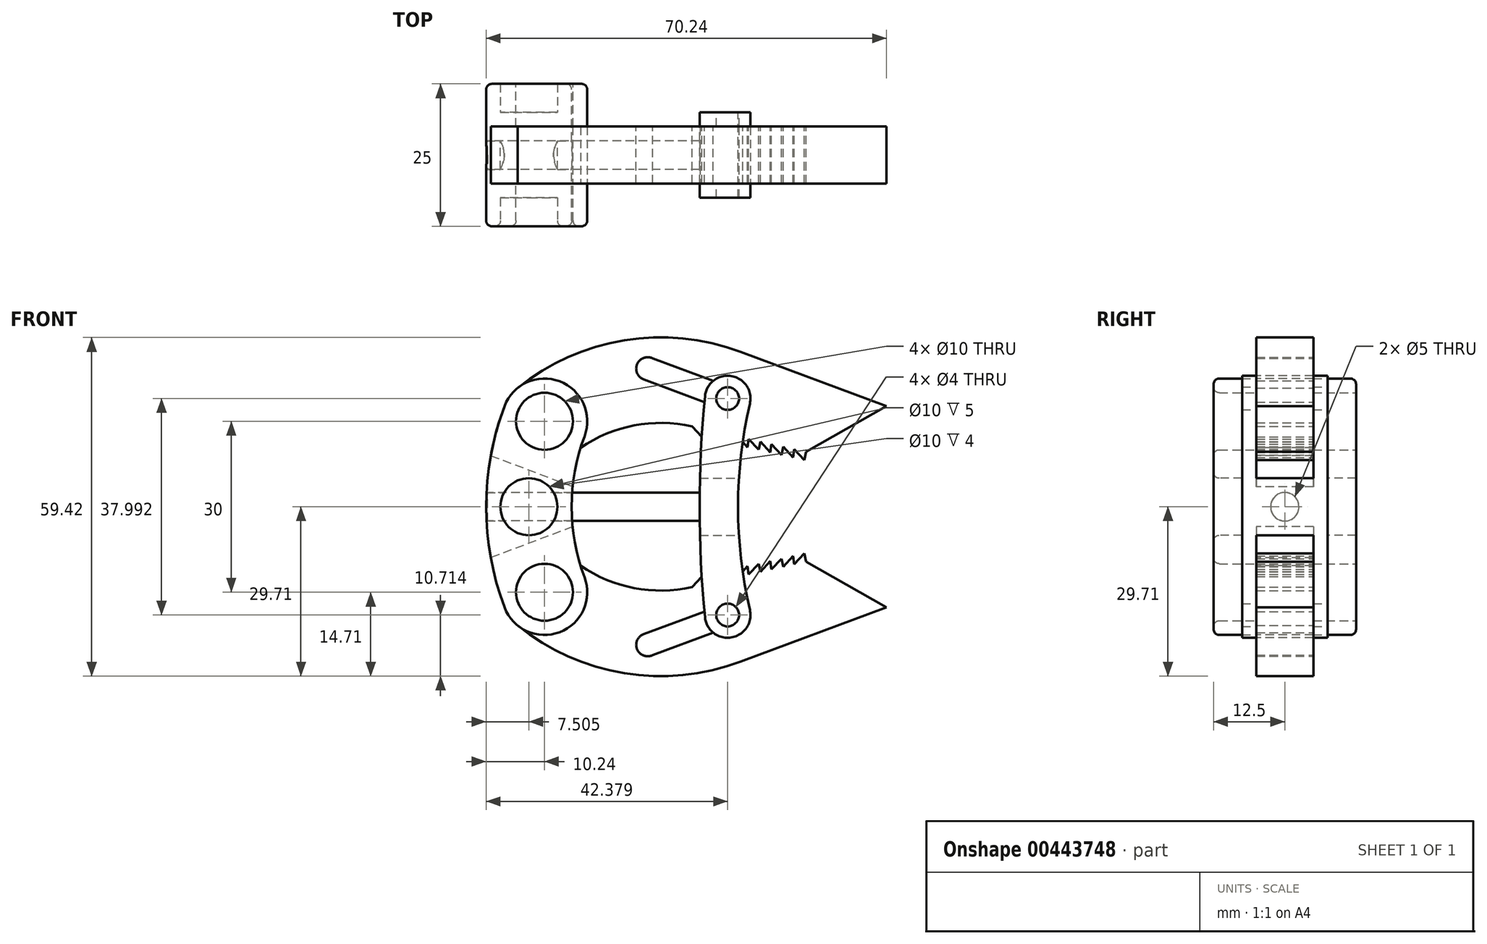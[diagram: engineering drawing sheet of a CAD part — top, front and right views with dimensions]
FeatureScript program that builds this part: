
annotation { "Feature Type Name" : "Feature", "Feature Type Description" : "" }
export const myFeature = defineFeature(function(context is Context, id is Id, definition is map)
    precondition{}
    {
        {
            var Q0;
            Q0=qCreatedBy(makeId("Front.planeOp"),FACE);
            var sketch = newSketch(context, id + "F0", { "sketchPlane" : qUnion([Q0])});
            skLineSegment(sketch, "E0", {"start": v(0, 15) * mm, "end": v(0, -15) * mm, "construction": true});
            skLineSegment(sketch, "E1", {"start": v(0, 0) * mm, "end": v(80, 0) * mm, "construction": true});
            skCircle(sketch, "E2", {"center": v(0, 15) * mm, "radius": 5 * mm});
            skCircle(sketch, "E3", {"center": v(0, -15) * mm, "radius": 5 * mm});
            skArc(sketch, "E4.0", {"start": v(7.02, 12.35) * mm, "mid": v(2.65, 22.02) * mm, "end": v(-7.02, 17.65) * mm});
            skArc(sketch, "E5.0", {"start": v(-7.02, -17.65) * mm, "mid": v(2.65, -22.02) * mm, "end": v(7.02, -12.35) * mm});
            skArc(sketch, "E6", {"start": v(-7.02, 17.65) * mm, "mid": v(-10.24, 0) * mm, "end": v(-7.02, -17.65) * mm});
            skArc(sketch, "E7", {"start": v(7.02, 12.35) * mm, "mid": v(4.76, 0) * mm, "end": v(7.02, -12.35) * mm});
            skSolve(sketch);
        }
        {
            var Q0;
            Q0=qCreatedBy(makeId("Front.planeOp"),FACE);
            var sketch = newSketch(context, id + "F1", { "sketchPlane" : qUnion([Q0])});
            skCircle(sketch, "E8.0", {"center": v(0, 15) * mm, "radius": 5 * mm});
            skCircle(sketch, "E9", {"center": v(0, 15) * mm, "radius": 7.5 * mm});
            skCircle(sketch, "E10.0", {"center": v(0, -15) * mm, "radius": 5 * mm});
            skCircle(sketch, "E11", {"center": v(0, -15) * mm, "radius": 7.5 * mm});
            skArc(sketch, "E12", {"start": v(34.4, 27.19) * mm, "mid": v(14, 29.2) * mm, "end": v(-4.71, 20.84) * mm});
            skLineSegment(sketch, "E13", {"start": v(34.4, 27.19) * mm, "end": v(60, 17.63) * mm});
            skLineSegment(sketch, "E14", {"start": v(60, 17.63) * mm, "end": v(45.88, 9.63) * mm});
            skLineSegment(sketch, "E15", {"start": v(45.88, 9.63) * mm, "end": v(25.88, 14.11) * mm});
            skArc(sketch, "E16", {"start": v(25.88, 14.11) * mm, "mid": v(14.73, 14.06) * mm, "end": v(4.71, 9.16) * mm});
            skLineSegment(sketch, "E17", {"start": v(34.4, 27.19) * mm, "end": v(32.14, 19) * mm, "construction": true});
            skLineSegment(sketch, "E18", {"start": v(32.14, 19) * mm, "end": v(18.09, 24.24) * mm, "construction": true});
            skArc(sketch, "E19.MirrorCS", {"start": v(34.4, -27.19) * mm, "mid": v(14, -29.2) * mm, "end": v(-4.71, -20.84) * mm});
            skLineSegment(sketch, "E20.MirrorCS", {"start": v(34.4, -27.19) * mm, "end": v(60, -17.63) * mm});
            skLineSegment(sketch, "E21.MirrorCS", {"start": v(45.88, -9.63) * mm, "end": v(25.88, -14.11) * mm});
            skLineSegment(sketch, "E22.MirrorCS", {"start": v(60, -17.63) * mm, "end": v(45.88, -9.63) * mm});
            skArc(sketch, "E23.MirrorCS", {"start": v(25.88, -14.11) * mm, "mid": v(14.73, -14.06) * mm, "end": v(4.71, -9.16) * mm});
            skLineSegment(sketch, "E24.MirrorCS", {"start": v(32.14, -19) * mm, "end": v(18.09, -24.24) * mm, "construction": true});
            skLineSegment(sketch, "E25.MirrorCS", {"start": v(34.4, -27.19) * mm, "end": v(32.14, -19) * mm, "construction": true});
            skArc(sketch, "E26", {"start": v(18.96, 26.04) * mm, "mid": v(16.25, 25.03) * mm, "end": v(17.39, 22.37) * mm});
            skArc(sketch, "E27", {"start": v(31.44, 17.12) * mm, "mid": v(34.04, 18.38) * mm, "end": v(32.67, 20.92) * mm});
            skLineSegment(sketch, "E28", {"start": v(18.96, 26.04) * mm, "end": v(32.84, 20.87) * mm});
            skLineSegment(sketch, "E29", {"start": v(17.39, 22.37) * mm, "end": v(31.44, 17.12) * mm});
            skLineSegment(sketch, "E30.MirrorCS", {"start": v(18.96, -26.04) * mm, "end": v(32.84, -20.87) * mm});
            skLineSegment(sketch, "E31.MirrorCS", {"start": v(17.39, -22.37) * mm, "end": v(31.44, -17.12) * mm});
            skArc(sketch, "E32.MirrorCS", {"start": v(18.96, -26.04) * mm, "mid": v(16.25, -25.03) * mm, "end": v(17.39, -22.37) * mm});
            skArc(sketch, "E33.MirrorCS", {"start": v(31.44, -17.12) * mm, "mid": v(34.04, -18.38) * mm, "end": v(32.67, -20.92) * mm});
            skLineSegment(sketch, "E34", {"start": v(25.88, 14.11) * mm, "end": v(27.61, 12.21) * mm});
            skLineSegment(sketch, "E35", {"start": v(27.61, 12.21) * mm, "end": v(27.83, 13.67) * mm});
            skLineSegment(sketch, "E36", {"start": v(27.83, 13.67) * mm, "end": v(29.57, 11.8) * mm});
            skLineSegment(sketch, "E37", {"start": v(29.57, 11.8) * mm, "end": v(29.88, 13.21) * mm});
            skLineSegment(sketch, "E38.1.0.0", {"start": v(31.6, 11.32) * mm, "end": v(31.83, 12.78) * mm});
            skLineSegment(sketch, "E38.1.0.1", {"start": v(29.88, 13.22) * mm, "end": v(31.6, 11.32) * mm});
            skLineSegment(sketch, "E38.1.0.2", {"start": v(31.83, 12.78) * mm, "end": v(33.57, 10.9) * mm});
            skLineSegment(sketch, "E38.1.0.3", {"start": v(33.57, 10.9) * mm, "end": v(33.88, 12.32) * mm});
            skLineSegment(sketch, "E38.2.0.0", {"start": v(35.6, 10.42) * mm, "end": v(35.83, 11.88) * mm});
            skLineSegment(sketch, "E38.2.0.1", {"start": v(33.87, 12.32) * mm, "end": v(35.6, 10.42) * mm});
            skLineSegment(sketch, "E38.2.0.2", {"start": v(35.83, 11.88) * mm, "end": v(37.56, 10) * mm});
            skLineSegment(sketch, "E38.2.0.3", {"start": v(37.56, 10) * mm, "end": v(37.88, 11.42) * mm});
            skLineSegment(sketch, "E38.3.0.0", {"start": v(39.6, 9.53) * mm, "end": v(39.82, 10.99) * mm});
            skLineSegment(sketch, "E38.3.0.1", {"start": v(37.87, 11.43) * mm, "end": v(39.6, 9.53) * mm});
            skLineSegment(sketch, "E38.3.0.2", {"start": v(39.82, 10.99) * mm, "end": v(41.56, 9.11) * mm});
            skLineSegment(sketch, "E38.3.0.3", {"start": v(41.56, 9.11) * mm, "end": v(41.88, 10.53) * mm});
            skLineSegment(sketch, "E38.4.0.0", {"start": v(43.6, 8.63) * mm, "end": v(43.82, 10.1) * mm});
            skLineSegment(sketch, "E38.4.0.1", {"start": v(41.87, 10.53) * mm, "end": v(43.6, 8.63) * mm});
            skLineSegment(sketch, "E38.4.0.2", {"start": v(43.82, 10.1) * mm, "end": v(45.56, 8.22) * mm});
            skLineSegment(sketch, "E38.4.0.3", {"start": v(45.56, 8.22) * mm, "end": v(45.88, 9.63) * mm});
            skLineSegment(sketch, "E38.direction1", {"start": v(27.61, 12.21) * mm, "end": v(31.6, 11.32) * mm, "construction": true});
            skLineSegment(sketch, "E39.MirrorCS", {"start": v(45.56, -8.22) * mm, "end": v(45.88, -9.63) * mm});
            skLineSegment(sketch, "E40.MirrorCS", {"start": v(43.82, -10.1) * mm, "end": v(45.56, -8.22) * mm});
            skLineSegment(sketch, "E41.MirrorCS", {"start": v(43.6, -8.63) * mm, "end": v(43.82, -10.1) * mm});
            skLineSegment(sketch, "E42.MirrorCS", {"start": v(41.87, -10.53) * mm, "end": v(43.6, -8.63) * mm});
            skLineSegment(sketch, "E43.MirrorCS", {"start": v(41.56, -9.11) * mm, "end": v(41.88, -10.53) * mm});
            skLineSegment(sketch, "E44.MirrorCS", {"start": v(39.82, -10.99) * mm, "end": v(41.56, -9.11) * mm});
            skLineSegment(sketch, "E45.MirrorCS", {"start": v(39.6, -9.53) * mm, "end": v(39.82, -10.99) * mm});
            skLineSegment(sketch, "E46.MirrorCS", {"start": v(37.87, -11.43) * mm, "end": v(39.6, -9.53) * mm});
            skLineSegment(sketch, "E47.MirrorCS", {"start": v(37.56, -10) * mm, "end": v(37.88, -11.42) * mm});
            skLineSegment(sketch, "E48.MirrorCS", {"start": v(35.83, -11.88) * mm, "end": v(37.56, -10) * mm});
            skLineSegment(sketch, "E49.MirrorCS", {"start": v(35.6, -10.42) * mm, "end": v(35.83, -11.88) * mm});
            skLineSegment(sketch, "E50.MirrorCS", {"start": v(33.87, -12.32) * mm, "end": v(35.6, -10.42) * mm});
            skLineSegment(sketch, "E51.MirrorCS", {"start": v(33.57, -10.9) * mm, "end": v(33.88, -12.32) * mm});
            skLineSegment(sketch, "E52.MirrorCS", {"start": v(31.83, -12.78) * mm, "end": v(33.57, -10.9) * mm});
            skLineSegment(sketch, "E53.MirrorCS", {"start": v(31.6, -11.32) * mm, "end": v(31.83, -12.78) * mm});
            skLineSegment(sketch, "E54.MirrorCS", {"start": v(29.88, -13.22) * mm, "end": v(31.6, -11.32) * mm});
            skLineSegment(sketch, "E55.MirrorCS", {"start": v(29.57, -11.8) * mm, "end": v(29.88, -13.21) * mm});
            skLineSegment(sketch, "E56.MirrorCS", {"start": v(27.83, -13.67) * mm, "end": v(29.57, -11.8) * mm});
            skLineSegment(sketch, "E57.MirrorCS", {"start": v(27.61, -12.21) * mm, "end": v(27.83, -13.67) * mm});
            skLineSegment(sketch, "E58.MirrorCS", {"start": v(25.88, -14.11) * mm, "end": v(27.61, -12.21) * mm});
            skSolve(sketch);
        }
        {
            var Q0;
            Q0 = qSketchRegion(id + "F1", true);
            extrude(context, id + "F2", {"entities" : qUnion([Q0]), "endBound" : BoundingType.SYMMETRIC, "depth" : 10 * mm});
        }
        {
            var Q0;
            Q0 = qSketchRegion(id + "F0", true);
            extrude(context, id + "F3", {"entities" : qUnion([Q0]), "endBound" : BoundingType.SYMMETRIC, "depth" : 25 * mm});
        }
        {
            var Q0;
            Q0=makeQuery(id+"F3.opExtrude","CAP_FACE",FACE,{"disambiguationData":[OSD([sQuery(id+"F0.wireOp",EDGE,"E2"),sQuery(id+"F0.wireOp",EDGE,"E3"),sQuery(id+"F0.wireOp",EDGE,"E4.0"),sQuery(id+"F0.wireOp",EDGE,"E5.0"),sQuery(id+"F0.wireOp",EDGE,"E6"),sQuery(id+"F0.wireOp",EDGE,"E7")])],"isStart":false});
            var sketch = newSketch(context, id + "F4", { "sketchPlane" : qUnion([Q0])});
            skArc(sketch, "E59", {"start": v(0, 15) * mm, "mid": v(-2.74, 0) * mm, "end": v(0, -15) * mm, "construction": true});
            skCircle(sketch, "E60", {"center": v(-2.74, 0) * mm, "radius": 5 * mm});
            skSolve(sketch);
        }
        {
            var Q0;
            Q0 = qSketchRegion(id + "F4", true);
            extrude(context, id + "F5", {"entities" : qUnion([Q0]), "operationType" : NewBodyOperationType.REMOVE, "endBound" : BoundingType.THROUGH_ALL, "oppositeDirection" : true, "depth" : 10 * mm});
        }
        {
            var Q0;
            Q0=qCreatedBy(makeId("Front.planeOp"),FACE);
            var sketch = newSketch(context, id + "F6", { "sketchPlane" : qUnion([Q0])});
            skCircle(sketch, "E61", {"center": v(-2.74, 0) * mm, "radius": 6 * mm, "construction": true});
            skCircle(sketch, "E62", {"center": v(0, -15) * mm, "radius": 9 * mm, "construction": true});
            skLineSegment(sketch, "E63", {"start": v(4.94, 3.52) * mm, "end": v(-9.43, 8.94) * mm});
            skLineSegment(sketch, "E64", {"start": v(4.94, -3.52) * mm, "end": v(-9.43, -8.94) * mm});
            skArc(sketch, "E65.0", {"start": v(-7.02, 17.65) * mm, "mid": v(-8.42, 13.35) * mm, "end": v(-9.43, 8.94) * mm});
            skArc(sketch, "E66.0", {"start": v(7.02, 12.35) * mm, "mid": v(5.7, 8) * mm, "end": v(4.94, 3.52) * mm});
            skLineSegment(sketch, "E67", {"start": v(-2.74, 0) * mm, "end": v(16.53, 0) * mm, "construction": true});
            skArc(sketch, "E68.0", {"start": v(7.02, 12.35) * mm, "mid": v(2.65, 22.02) * mm, "end": v(-7.02, 17.65) * mm});
            skArc(sketch, "E69.0", {"start": v(-7.02, -17.65) * mm, "mid": v(2.65, -22.02) * mm, "end": v(7.02, -12.35) * mm});
            skArc(sketch, "E70.trimOffspring", {"start": v(4.94, -3.52) * mm, "mid": v(5.7, -8) * mm, "end": v(7.02, -12.35) * mm});
            skArc(sketch, "E71.trimOffspring", {"start": v(-9.43, -8.94) * mm, "mid": v(-8.42, -13.35) * mm, "end": v(-7.02, -17.65) * mm});
            skSolve(sketch);
        }
        {
            var Q0;
            Q0 = qSketchRegion(id + "F6", true);
            extrude(context, id + "F7", {"entities" : qUnion([Q0]), "operationType" : NewBodyOperationType.REMOVE, "endBound" : BoundingType.SYMMETRIC, "oppositeDirection" : true, "depth" : 10 * mm});
        }
        {
            var Q0;
            Q0=qCreatedBy(makeId("Front.planeOp"),FACE);
            var sketch = newSketch(context, id + "F8", { "sketchPlane" : qUnion([Q0])});
            skCircle(sketch, "E72.0", {"center": v(-2.74, 0) * mm, "radius": 5 * mm});
            skSolve(sketch);
        }
        {
            var Q0;
            Q0=qCreatedBy(makeId("Right.planeOp"),FACE);
            var sketch = newSketch(context, id + "F9", { "sketchPlane" : qUnion([Q0])});
            skCircle(sketch, "E73", {"center": v(0, 0) * mm, "radius": 2.5 * mm});
            skSolve(sketch);
        }
        {
            var Q0;
            Q0 = qSketchRegion(id + "F9", true);
            extrude(context, id + "F10", {"entities" : qUnion([Q0]), "operationType" : NewBodyOperationType.REMOVE, "endBound" : BoundingType.THROUGH_ALL, "oppositeDirection" : true, "depth" : 25 * mm, "hasSecondDirection" : true, "secondDirectionBound" : SecondDirectionBoundingType.THROUGH_ALL, "secondDirectionOppositeDirection" : false, "secondDirectionDepth" : 25 * mm});
        }
        {
            var Q0;
            Q0=qCreatedBy(makeId("Front.planeOp"),FACE);
            var sketch = newSketch(context, id + "F11", { "sketchPlane" : qUnion([Q0])});
            skPoint(sketch, "E74.0", {"position": v(34.01, 18.3) * mm});
            skPoint(sketch, "E75.0", {"position": v(34.01, -18.3) * mm});
            skArc(sketch, "E76", {"start": v(36.03, 18.1) * mm, "mid": v(32.79, 22.94) * mm, "end": v(28.16, 19.38) * mm});
            skLineSegment(sketch, "E77", {"start": v(0, 0) * mm, "end": v(41.87, 0) * mm, "construction": true});
            skArc(sketch, "E78.MirrorC", {"start": v(36.03, -18.1) * mm, "mid": v(32.79, -22.94) * mm, "end": v(28.16, -19.38) * mm});
            skArc(sketch, "E79", {"start": v(28.16, 19.38) * mm, "mid": v(27.22, 0) * mm, "end": v(28.16, -19.38) * mm});
            skArc(sketch, "E80", {"start": v(36.03, 18.1) * mm, "mid": v(33.96, 0) * mm, "end": v(36.03, -18.1) * mm});
            skArc(sketch, "E81.0", {"start": v(31.44, 17.12) * mm, "mid": v(34.01, 18.3) * mm, "end": v(32.84, 20.87) * mm});
            skCircle(sketch, "E82", {"center": v(32.14, 19) * mm, "radius": 2 * mm});
            skArc(sketch, "E83.0", {"start": v(31.44, -17.12) * mm, "mid": v(34.01, -18.3) * mm, "end": v(32.84, -20.87) * mm});
            skCircle(sketch, "E84.MirrorC", {"center": v(32.14, -19) * mm, "radius": 2 * mm});
            skSolve(sketch);
        }
        {
            var Q0;
            Q0=qCreatedBy(makeId("Front.planeOp"),FACE);
            var sketch = newSketch(context, id + "F12", { "sketchPlane" : qUnion([Q0])});
            skLineSegment(sketch, "E85", {"start": v(27.28, -5) * mm, "end": v(27.28, -5) * mm});
            skLineSegment(sketch, "E86.MirrorCS", {"start": v(27.28, 5) * mm, "end": v(34.12, 5) * mm});
            skPoint(sketch, "E87.orphan", {"position": v(28.16, -19.38) * mm});
            skPoint(sketch, "E88.orphan", {"position": v(36.03, -18.1) * mm});
            skPoint(sketch, "E89.orphan", {"position": v(36.03, 18.1) * mm});
            skPoint(sketch, "E90.orphan", {"position": v(28.16, 19.38) * mm});
            skArc(sketch, "E91.0", {"start": v(36.03, 18.1) * mm, "mid": v(34.8, 11.59) * mm, "end": v(34.12, 5) * mm});
            skArc(sketch, "E91.1", {"start": v(28.16, 19.38) * mm, "mid": v(27.59, 12.2) * mm, "end": v(27.28, 5) * mm});
            skArc(sketch, "E91.2", {"start": v(36.03, 18.1) * mm, "mid": v(32.79, 22.94) * mm, "end": v(28.16, 19.38) * mm});
            skArc(sketch, "E91.3", {"start": v(36.03, -18.1) * mm, "mid": v(32.79, -22.94) * mm, "end": v(28.16, -19.38) * mm});
            skLineSegment(sketch, "E92", {"start": v(27.28, -5) * mm, "end": v(34.12, -5) * mm});
            skArc(sketch, "E93", {"start": v(27.28, 5) * mm, "mid": v(27.22, 0) * mm, "end": v(27.28, -5) * mm, "construction": true});
            skArc(sketch, "E94", {"start": v(34.12, 5) * mm, "mid": v(33.96, 0) * mm, "end": v(34.12, -5) * mm, "construction": true});
            skArc(sketch, "E95", {"start": v(34.12, -5) * mm, "mid": v(34.8, -11.59) * mm, "end": v(36.03, -18.1) * mm});
            skArc(sketch, "E96", {"start": v(27.28, -5) * mm, "mid": v(27.59, -12.2) * mm, "end": v(28.16, -19.38) * mm});
            skSolve(sketch);
        }
        {
            var Q0;
            Q0 = qSketchRegion(id + "F8", true);
            extrude(context, id + "F13", {"entities" : qUnion([Q0]), "operationType" : NewBodyOperationType.ADD, "endBound" : BoundingType.SYMMETRIC, "depth" : 10 * mm});
        }
        {
            var Q0;
            Q0 = qSketchRegion(id + "F8", true);
            extrude(context, id + "F14", {"entities" : qUnion([Q0]), "operationType" : NewBodyOperationType.ADD, "endBound" : BoundingType.SYMMETRIC, "depth" : 15 * mm});
        }
        {
            var Q0;
            Q0 = qSketchRegion(id + "F9", true);
            extrude(context, id + "F15", {"entities" : qUnion([Q0]), "depth" : 32 * mm, "hasSecondDirection" : true, "secondDirectionOppositeDirection" : true, "secondDirectionDepth" : 10 * mm});
        }
        {
            var Q0;
            Q0 = qSketchRegion(id + "F11", true);
            extrude(context, id + "F16", {"entities" : qUnion([Q0]), "operationType" : NewBodyOperationType.ADD, "endBound" : BoundingType.SYMMETRIC, "depth" : 15 * mm});
        }
        {
            var Q0;
            Q0 = qSketchRegion(id + "F12", true);
            extrude(context, id + "F17", {"entities" : qUnion([Q0]), "operationType" : NewBodyOperationType.REMOVE, "endBound" : BoundingType.SYMMETRIC, "oppositeDirection" : true, "depth" : 10 * mm});
        }
        {
            var Q0;
            Q0=makeQuery(id+"F3.opExtrude","CAP_EDGE",EDGE,{"disambiguationData":[OSD([sQuery(id+"F0.wireOp",EDGE,"E7")])],"isStart":false});
            var Q1;
            Q1=makeQuery(id+"F3.opExtrude","CAP_EDGE",EDGE,{"disambiguationData":[OSD([sQuery(id+"F0.wireOp",EDGE,"E4.0")])],"isStart":false});
            var Q2;
            Q2=makeQuery(id+"F3.opExtrude","CAP_EDGE",EDGE,{"disambiguationData":[OSD([sQuery(id+"F0.wireOp",EDGE,"E6")])],"isStart":true});
            var Q3;
            Q3=makeQuery(id+"F3.opExtrude","CAP_EDGE",EDGE,{"disambiguationData":[OSD([sQuery(id+"F0.wireOp",EDGE,"E4.0")])],"isStart":true});
            var Q4;
            Q4=makeQuery(id+"F3.opExtrude","CAP_EDGE",EDGE,{"disambiguationData":[OSD([sQuery(id+"F0.wireOp",EDGE,"E7")])],"isStart":true});
            var Q5;
            Q5=makeQuery(id+"F3.opExtrude","CAP_EDGE",EDGE,{"disambiguationData":[OSD([sQuery(id+"F0.wireOp",EDGE,"E5.0")])],"isStart":true});
            var Q6;
            Q6=makeQuery(id+"F3.opExtrude","CAP_EDGE",EDGE,{"disambiguationData":[OSD([sQuery(id+"F0.wireOp",EDGE,"E6")])],"isStart":false});
            var Q7;
            Q7=makeQuery(id+"F3.opExtrude","CAP_FACE",FACE,{"disambiguationData":[OSD([sQuery(id+"F0.wireOp",EDGE,"E2"),sQuery(id+"F0.wireOp",EDGE,"E3"),sQuery(id+"F0.wireOp",EDGE,"E4.0"),sQuery(id+"F0.wireOp",EDGE,"E5.0"),sQuery(id+"F0.wireOp",EDGE,"E6"),sQuery(id+"F0.wireOp",EDGE,"E7")])],"isStart":false});
            var Q8;
            Q8=makeQuery(id+"F7.boolean.opBoolean","COPY",EDGE,{"derivedFrom":makeQuery(id+"F7.opExtrude","CAP_EDGE",EDGE,{"disambiguationData":[OSD([sQuery(id+"F6.wireOp",EDGE,"E70.trimOffspring")])],"isStart":true})});
            var Q9;
            Q9=makeQuery(id+"F7.boolean.opBoolean","COPY",EDGE,{"derivedFrom":makeQuery(id+"F7.opExtrude","SWEPT_EDGE",EDGE,{"disambiguationData":[OSD([sQuery(id+"F6.wireOp",EDGE,"E64"),sQuery(id+"F6.wireOp",EDGE,"E70.trimOffspring")])]})});
            var Q10;
            Q10=makeQuery(id+"F7.boolean.opBoolean","COPY",EDGE,{"derivedFrom":makeQuery(id+"F7.opExtrude","SWEPT_EDGE",EDGE,{"disambiguationData":[OSD([sQuery(id+"F6.wireOp",EDGE,"E63"),sQuery(id+"F6.wireOp",EDGE,"E66.0")])]})});
            var Q11;
            Q11=makeQuery(id+"F7.boolean.opBoolean","COPY",EDGE,{"derivedFrom":makeQuery(id+"F7.opExtrude","CAP_EDGE",EDGE,{"disambiguationData":[OSD([sQuery(id+"F6.wireOp",EDGE,"E66.0")])],"isStart":false})});
            var Q12;
            Q12=makeQuery(id+"F7.boolean.opBoolean","COPY",EDGE,{"derivedFrom":makeQuery(id+"F7.opExtrude","CAP_EDGE",EDGE,{"disambiguationData":[OSD([sQuery(id+"F6.wireOp",EDGE,"E70.trimOffspring")])],"isStart":false})});
            var Q13;
            Q13=makeQuery(id+"F7.boolean.opBoolean","COPY",EDGE,{"derivedFrom":makeQuery(id+"F7.opExtrude","CAP_EDGE",EDGE,{"disambiguationData":[OSD([sQuery(id+"F6.wireOp",EDGE,"E66.0")])],"isStart":true})});
            fillet(context, id + "F18", {"entities" : qUnion([Q0, Q1, Q2, Q3, Q4, Q5, Q6, Q7, Q8, Q9, Q10, Q11, Q12, Q13]), "radius" : 1 * mm, "tangentPropagation" : true, "allowEdgeOverflow" : false});
        }
    });
